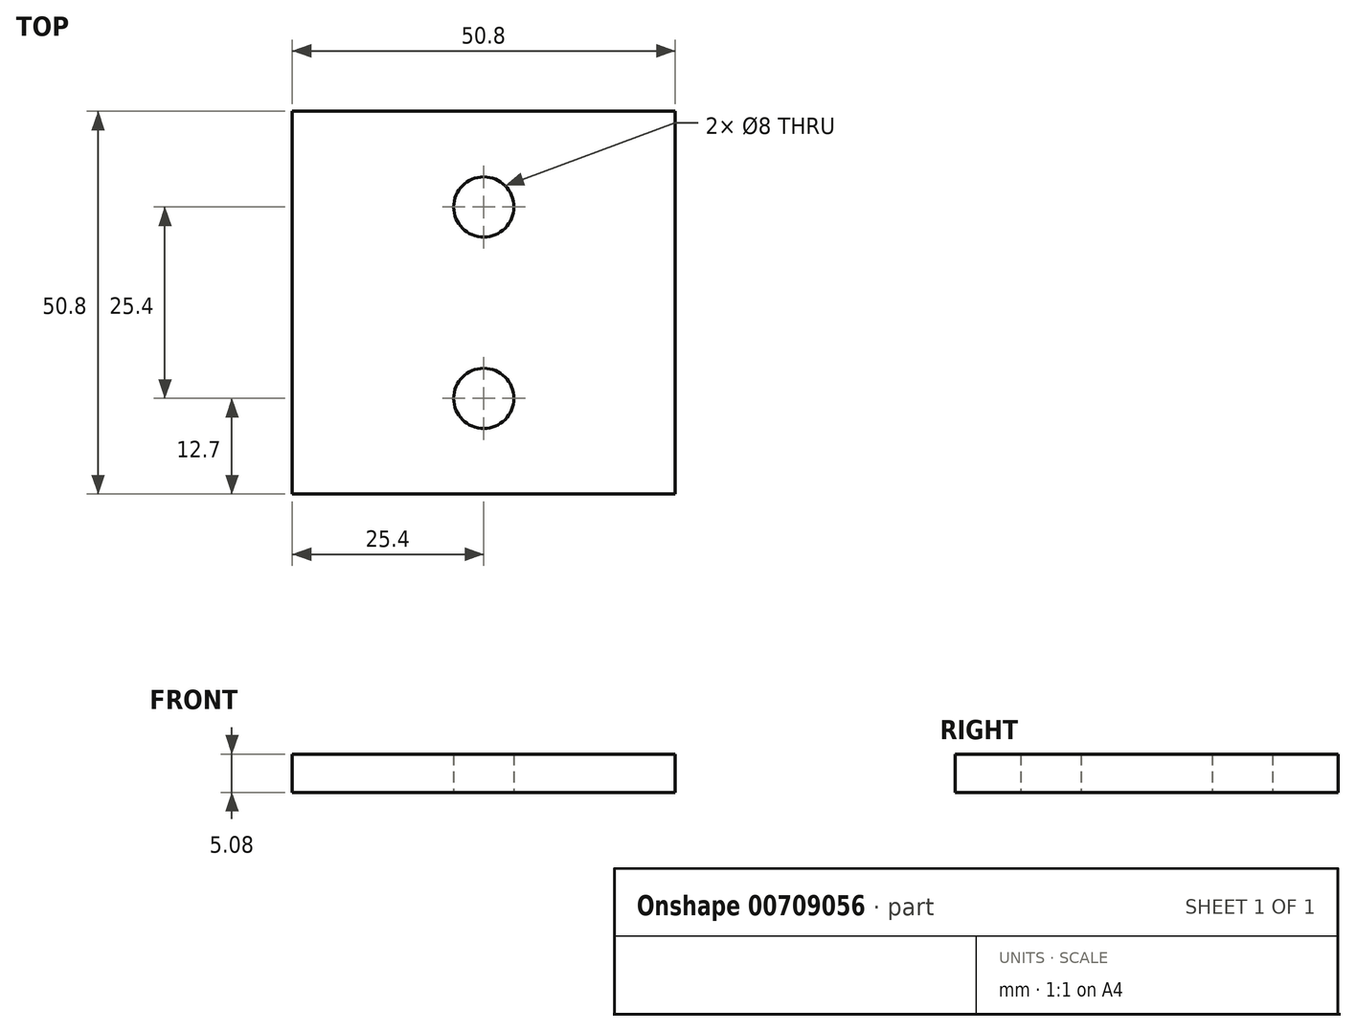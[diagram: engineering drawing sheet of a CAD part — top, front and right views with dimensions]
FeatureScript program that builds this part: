
annotation { "Feature Type Name" : "Feature", "Feature Type Description" : "" }
export const myFeature = defineFeature(function(context is Context, id is Id, definition is map)
    precondition{}
    {
        {
            var Q0;
            Q0=qCreatedBy(makeId("Top.planeOp"),FACE);
            var sketch = newSketch(context, id + "F0", { "sketchPlane" : qUnion([Q0])});
            skLineSegment(sketch, "E0.bottom", {"start": v(0, 0) * mm, "end": v(50.8, 0) * mm});
            skLineSegment(sketch, "E0.top", {"start": v(0, -50.8) * mm, "end": v(50.8, -50.8) * mm});
            skLineSegment(sketch, "E0.left", {"start": v(0, 0) * mm, "end": v(0, -50.8) * mm});
            skLineSegment(sketch, "E0.right", {"start": v(50.8, 0) * mm, "end": v(50.8, -50.8) * mm});
            skCircle(sketch, "E1", {"center": v(25.4, -12.7) * mm, "radius": 4 * mm});
            skLineSegment(sketch, "E2", {"start": v(25.4, 0) * mm, "end": v(25.4, -12.7) * mm, "construction": true});
            skCircle(sketch, "E3", {"center": v(25.4, -38.1) * mm, "radius": 4 * mm});
            skSolve(sketch);
        }
        {
            var Q0;
            Q0=makeQuery(id+"F0.imprint","IMPRINT",FACE,{"disambiguationData":[TD([[makeQuery(id+"F0.imprint","IMPRINT",EDGE,{"derivedFrom":sQuery(id+"F0.wireOp",EDGE,"E0.bottom")}),-1.0]])]});
            extrude(context, id + "F1", {"entities" : qUnion([Q0]), "depth" : 5.08 * mm, "offsetDistance" : 25.4 * mm});
        }
    });
